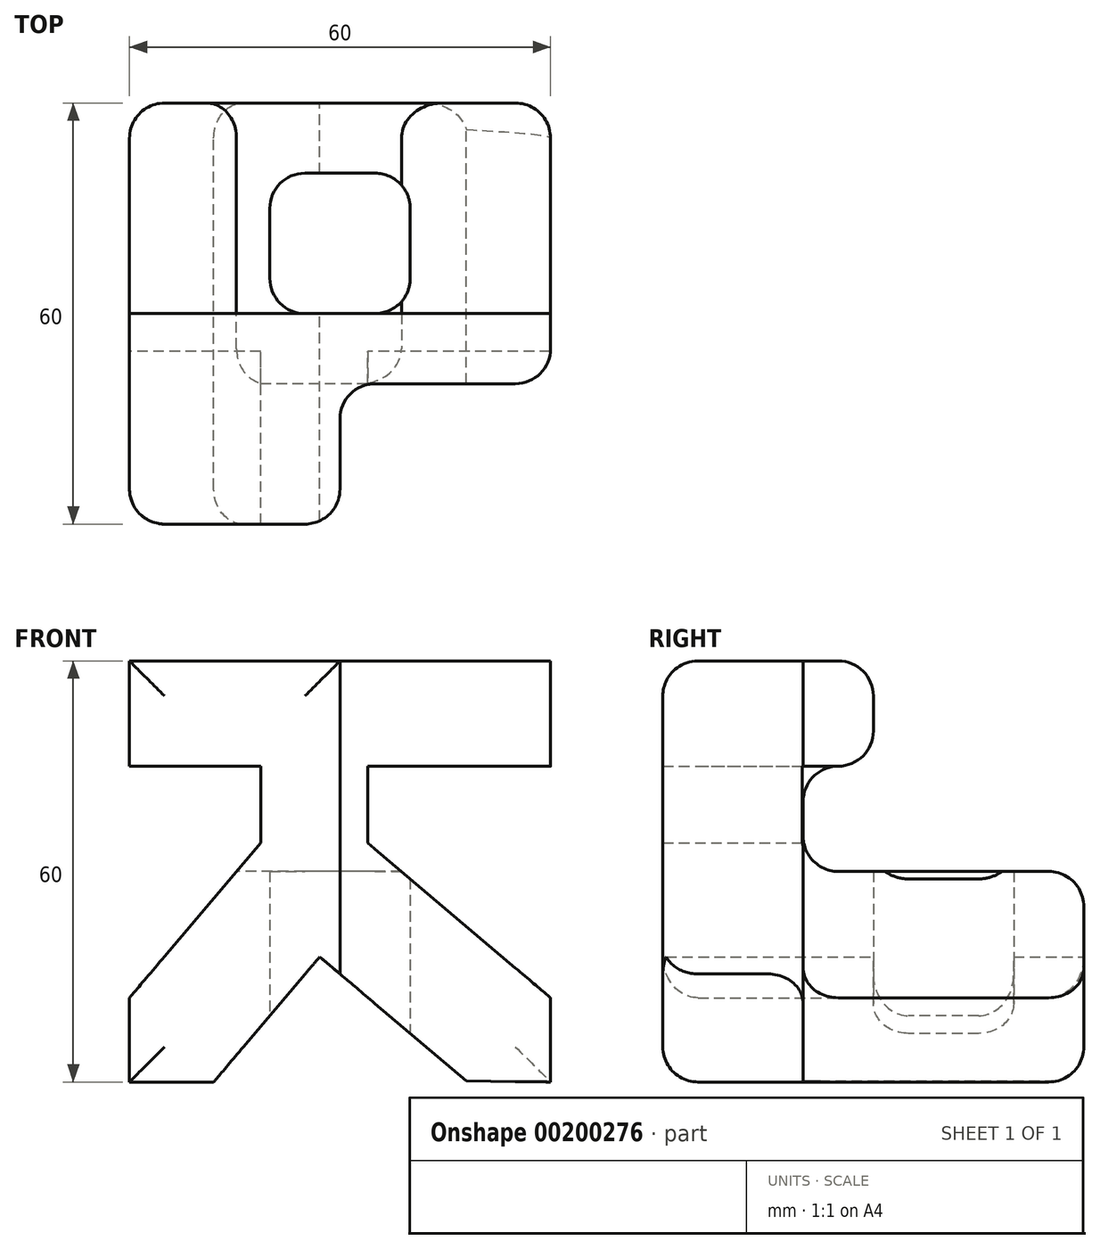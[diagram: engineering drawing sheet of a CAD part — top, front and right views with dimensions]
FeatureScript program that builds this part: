
annotation { "Feature Type Name" : "Feature", "Feature Type Description" : "" }
export const myFeature = defineFeature(function(context is Context, id is Id, definition is map)
    precondition{}
    {
        {
            var Q0;
            Q0=qCreatedBy(makeId("Top.planeOp"),FACE);
            var sketch = newSketch(context, id + "F0", { "sketchPlane" : qUnion([Q0])});
            skLineSegment(sketch, "E0.bottom", {"start": v(-30, 30) * mm, "end": v(30, 30) * mm, "construction": true});
            skLineSegment(sketch, "E0.top", {"start": v(-30, -30) * mm, "end": v(30, -30) * mm, "construction": true});
            skLineSegment(sketch, "E0.left", {"start": v(-30, 30) * mm, "end": v(-30, -30) * mm, "construction": true});
            skLineSegment(sketch, "E0.right", {"start": v(30, 30) * mm, "end": v(30, -30) * mm, "construction": true});
            skLineSegment(sketch, "E1.bottom", {"start": v(-25, 30) * mm, "end": v(25, 30) * mm});
            skLineSegment(sketch, "E1.top", {"start": v(-25, -30) * mm, "end": v(-5, -30) * mm});
            skLineSegment(sketch, "E1.left", {"start": v(-30, 25) * mm, "end": v(-30, -25) * mm});
            skLineSegment(sketch, "E1.right", {"start": v(30, 25) * mm, "end": v(30, -5) * mm});
            skLineSegment(sketch, "E2.top", {"start": v(25, -10) * mm, "end": v(5, -10) * mm});
            skLineSegment(sketch, "E2.right", {"start": v(0, -25) * mm, "end": v(0, -15) * mm});
            skLineSegment(sketch, "E3.bottom", {"start": v(-5, 0) * mm, "end": v(5, 0) * mm});
            skLineSegment(sketch, "E3.top", {"start": v(-5, 20) * mm, "end": v(5, 20) * mm});
            skLineSegment(sketch, "E3.left", {"start": v(-10, 5) * mm, "end": v(-10, 15) * mm});
            skLineSegment(sketch, "E3.right", {"start": v(10, 5) * mm, "end": v(10, 15) * mm});
            skPoint(sketch, "E4.visualSharp", {"position": v(-30, 30) * mm});
            skArc(sketch, "E4.filletArc", {"start": v(-25, 30) * mm, "mid": v(-28.54, 28.54) * mm, "end": v(-30, 25) * mm});
            skPoint(sketch, "E5.visualSharp", {"position": v(30, 30) * mm});
            skArc(sketch, "E5.filletArc", {"start": v(30, 25) * mm, "mid": v(28.54, 28.54) * mm, "end": v(25, 30) * mm});
            skPoint(sketch, "E6.visualSharp", {"position": v(30, -10) * mm});
            skArc(sketch, "E6.filletArc", {"start": v(25, -10) * mm, "mid": v(28.54, -8.54) * mm, "end": v(30, -5) * mm});
            skPoint(sketch, "E7.visualSharp", {"position": v(0, -10) * mm});
            skArc(sketch, "E7.filletArc", {"start": v(5, -10) * mm, "mid": v(1.46, -11.46) * mm, "end": v(0, -15) * mm});
            skPoint(sketch, "E8.visualSharp", {"position": v(0, -30) * mm});
            skArc(sketch, "E8.filletArc", {"start": v(-5, -30) * mm, "mid": v(-1.46, -28.54) * mm, "end": v(0, -25) * mm});
            skPoint(sketch, "E9.visualSharp", {"position": v(-30, -30) * mm});
            skArc(sketch, "E9.filletArc", {"start": v(-30, -25) * mm, "mid": v(-28.54, -28.54) * mm, "end": v(-25, -30) * mm});
            skPoint(sketch, "E10.visualSharp", {"position": v(-10, 0) * mm});
            skArc(sketch, "E10.filletArc", {"start": v(-10, 5) * mm, "mid": v(-8.54, 1.46) * mm, "end": v(-5, 0) * mm});
            skPoint(sketch, "E11.visualSharp", {"position": v(-10, 20) * mm});
            skArc(sketch, "E11.filletArc", {"start": v(-5, 20) * mm, "mid": v(-8.54, 18.54) * mm, "end": v(-10, 15) * mm});
            skPoint(sketch, "E12.visualSharp", {"position": v(10, 20) * mm});
            skArc(sketch, "E12.filletArc", {"start": v(10, 15) * mm, "mid": v(8.54, 18.54) * mm, "end": v(5, 20) * mm});
            skPoint(sketch, "E13.visualSharp", {"position": v(10, 0) * mm});
            skArc(sketch, "E13.filletArc", {"start": v(5, 0) * mm, "mid": v(8.54, 1.46) * mm, "end": v(10, 5) * mm});
            skSolve(sketch);
        }
        {
            var Q0;
            Q0 = qSketchRegion(id + "F0", true);
            extrude(context, id + "F1", {"entities" : qUnion([Q0]), "endBound" : BoundingType.SYMMETRIC, "depth" : 60 * mm});
        }
        {
            var Q0;
            Q0=qCreatedBy(makeId("Right.planeOp"),FACE);
            var sketch = newSketch(context, id + "F2", { "sketchPlane" : qUnion([Q0])});
            skLineSegment(sketch, "E14.bottom", {"start": v(0, 30) * mm, "end": v(-30, 30) * mm, "construction": true});
            skLineSegment(sketch, "E14.left", {"start": v(30, -25) * mm, "end": v(30, -30) * mm, "construction": true});
            skLineSegment(sketch, "E14.right", {"start": v(-30, 30) * mm, "end": v(-30, -30) * mm, "construction": true});
            skLineSegment(sketch, "E15", {"start": v(-30, 25) * mm, "end": v(-30, -25) * mm});
            skLineSegment(sketch, "E16", {"start": v(30, -25) * mm, "end": v(30, -5) * mm});
            skLineSegment(sketch, "E17", {"start": v(25, 0) * mm, "end": v(-5, 0) * mm});
            skLineSegment(sketch, "E18", {"start": v(-10, 5) * mm, "end": v(-10, 10) * mm});
            skLineSegment(sketch, "E19", {"start": v(-5, 15) * mm, "end": v(-5, 15) * mm});
            skLineSegment(sketch, "E20", {"start": v(0, 20) * mm, "end": v(0, 25) * mm});
            skLineSegment(sketch, "E21", {"start": v(-5, 30) * mm, "end": v(-25, 30) * mm});
            skPoint(sketch, "E22.orphan", {"position": v(30, 30) * mm});
            skLineSegment(sketch, "E23", {"start": v(25, -30) * mm, "end": v(-25, -30) * mm});
            skPoint(sketch, "E24.visualSharp", {"position": v(-10, 0) * mm});
            skArc(sketch, "E24.filletArc", {"start": v(-10, 5) * mm, "mid": v(-8.54, 1.46) * mm, "end": v(-5, 0) * mm});
            skPoint(sketch, "E25.visualSharp", {"position": v(-10, 15) * mm});
            skArc(sketch, "E25.filletArc", {"start": v(-5, 15) * mm, "mid": v(-8.54, 13.54) * mm, "end": v(-10, 10) * mm});
            skPoint(sketch, "E26.visualSharp", {"position": v(0, 15) * mm});
            skArc(sketch, "E26.filletArc", {"start": v(-5, 15) * mm, "mid": v(-1.46, 16.46) * mm, "end": v(0, 20) * mm});
            skPoint(sketch, "E27.visualSharp", {"position": v(0, 30) * mm});
            skArc(sketch, "E27.filletArc", {"start": v(0, 25) * mm, "mid": v(-1.46, 28.54) * mm, "end": v(-5, 30) * mm});
            skPoint(sketch, "E28.visualSharp", {"position": v(-30, 30) * mm});
            skArc(sketch, "E28.filletArc", {"start": v(-25, 30) * mm, "mid": v(-28.54, 28.54) * mm, "end": v(-30, 25) * mm});
            skPoint(sketch, "E29.visualSharp", {"position": v(-30, -30) * mm});
            skArc(sketch, "E29.filletArc", {"start": v(-30, -25) * mm, "mid": v(-28.54, -28.54) * mm, "end": v(-25, -30) * mm});
            skPoint(sketch, "E30.visualSharp", {"position": v(30, -30) * mm});
            skArc(sketch, "E30.filletArc", {"start": v(25, -30) * mm, "mid": v(28.54, -28.54) * mm, "end": v(30, -25) * mm});
            skPoint(sketch, "E31.visualSharp", {"position": v(30, 0) * mm});
            skArc(sketch, "E31.filletArc", {"start": v(30, -5) * mm, "mid": v(28.54, -1.46) * mm, "end": v(25, 0) * mm});
            skSolve(sketch);
        }
        {
            var Q0;
            Q0 = qSketchRegion(id + "F2", true);
            extrude(context, id + "F3", {"entities" : qUnion([Q0]), "operationType" : NewBodyOperationType.INTERSECT, "endBound" : BoundingType.SYMMETRIC, "depth" : 60 * mm});
        }
        {
            var Q0;
            Q0=qCreatedBy(makeId("Front.planeOp"),FACE);
            var sketch = newSketch(context, id + "F4", { "sketchPlane" : qUnion([Q0])});
            skLineSegment(sketch, "E32.bottom", {"start": v(-30, 30) * mm, "end": v(30, 30) * mm, "construction": true});
            skLineSegment(sketch, "E32.top", {"start": v(-30, -30) * mm, "end": v(-18, -30) * mm, "construction": true});
            skLineSegment(sketch, "E32.left", {"start": v(-30, 30) * mm, "end": v(-30, 14.98) * mm, "construction": true});
            skLineSegment(sketch, "E32.right", {"start": v(30, 30) * mm, "end": v(30, 14.98) * mm, "construction": true});
            skLineSegment(sketch, "E33", {"start": v(-30, 30) * mm, "end": v(30, 30) * mm});
            skLineSegment(sketch, "E34", {"start": v(30, 14.98) * mm, "end": v(3.95, 14.98) * mm});
            skLineSegment(sketch, "E35", {"start": v(3.95, 14.98) * mm, "end": v(3.95, 4.07) * mm});
            skLineSegment(sketch, "E36", {"start": v(3.95, 4.07) * mm, "end": v(30, -18) * mm});
            skLineSegment(sketch, "E37", {"start": v(30, -18) * mm, "end": v(30, -30) * mm});
            skLineSegment(sketch, "E38", {"start": v(18, -29.85) * mm, "end": v(-2.89, -12.16) * mm});
            skLineSegment(sketch, "E39", {"start": v(-2.89, -12.16) * mm, "end": v(-18, -30) * mm});
            skLineSegment(sketch, "E40", {"start": v(-18, -30) * mm, "end": v(-30, -30) * mm});
            skLineSegment(sketch, "E41", {"start": v(-30, -18) * mm, "end": v(-11.3, 4.07) * mm});
            skLineSegment(sketch, "E42", {"start": v(-11.3, 4.07) * mm, "end": v(-11.3, 14.98) * mm});
            skLineSegment(sketch, "E43", {"start": v(-11.3, 14.98) * mm, "end": v(-30, 14.98) * mm});
            skLineSegment(sketch, "E44", {"start": v(-30, 14.98) * mm, "end": v(-30, 30) * mm});
            skLineSegment(sketch, "E45.trimOffspring", {"start": v(30, -18) * mm, "end": v(30, -30) * mm, "construction": true});
            skLineSegment(sketch, "E46", {"start": v(-30, -18) * mm, "end": v(-30, -30) * mm});
            skLineSegment(sketch, "E47", {"start": v(30, -30) * mm, "end": v(18, -29.85) * mm});
            skLineSegment(sketch, "E48", {"start": v(30, 30) * mm, "end": v(30, 14.98) * mm});
            skSolve(sketch);
        }
        {
            var Q0;
            Q0 = qSketchRegion(id + "F4", true);
            extrude(context, id + "F5", {"entities" : qUnion([Q0]), "operationType" : NewBodyOperationType.INTERSECT, "endBound" : BoundingType.SYMMETRIC, "depth" : 60 * mm});
        }
    });
